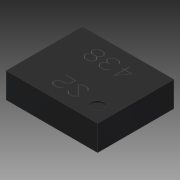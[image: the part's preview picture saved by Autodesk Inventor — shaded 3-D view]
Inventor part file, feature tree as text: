
AUTODESK INVENTOR PART (.ipt)
format: ipt  version: 2016 (Build 200138000, 138)  size: 309,248 bytes
history: native  units: mm
features: extrude x4, sketch x3, projected_geometry x2, chamfer x1
ambient origin geometry x8: Origin, YZ Plane, XZ Plane, XY Plane, X Axis, Y Axis, Z Axis, Center Point
bodies: Body1 (feature_tree)
feature tree (10):
  extrude  "Extrusion4"  Depth=3.0mm
  sketch  "Sketch11"  dims[d9=0.83mm d10=0.0mm d11=1.75mm]
  extrude  "Extrusion5"  Depth=1.75mm
  extrude  "Extrusion6"  Depth=0.2mm
  extrude  "Extrusion7"  Depth=0.5mm
  chamfer  "Chamfer1"  Distance=0.5mm
  sketch  "Sketch10"  dims[d7=2.5mm d8=3.0mm]
  projected_geometry  "Projected Loop1"
  sketch  "Sketch12"  dims[d12=1.0mm d13=0.4mm d14=0.5mm d15=0.5mm d16=0.01mm d17=0.0mm d18=0.05mm d19=0.0mm d20=30.0mm d22=0.5mm d23=10.0mm d25=10.0mm d27=40.0mm d29=0.5mm d30=10.0mm d32=10.0mm d34=0.02mm d35=0.0mm d36=0.1mm d37=0.1mm d38=0.55mm d39=0.35mm d40=0.2mm d41=2.0mm d42=45.0deg]
  projected_geometry  "Projected Loop2"
